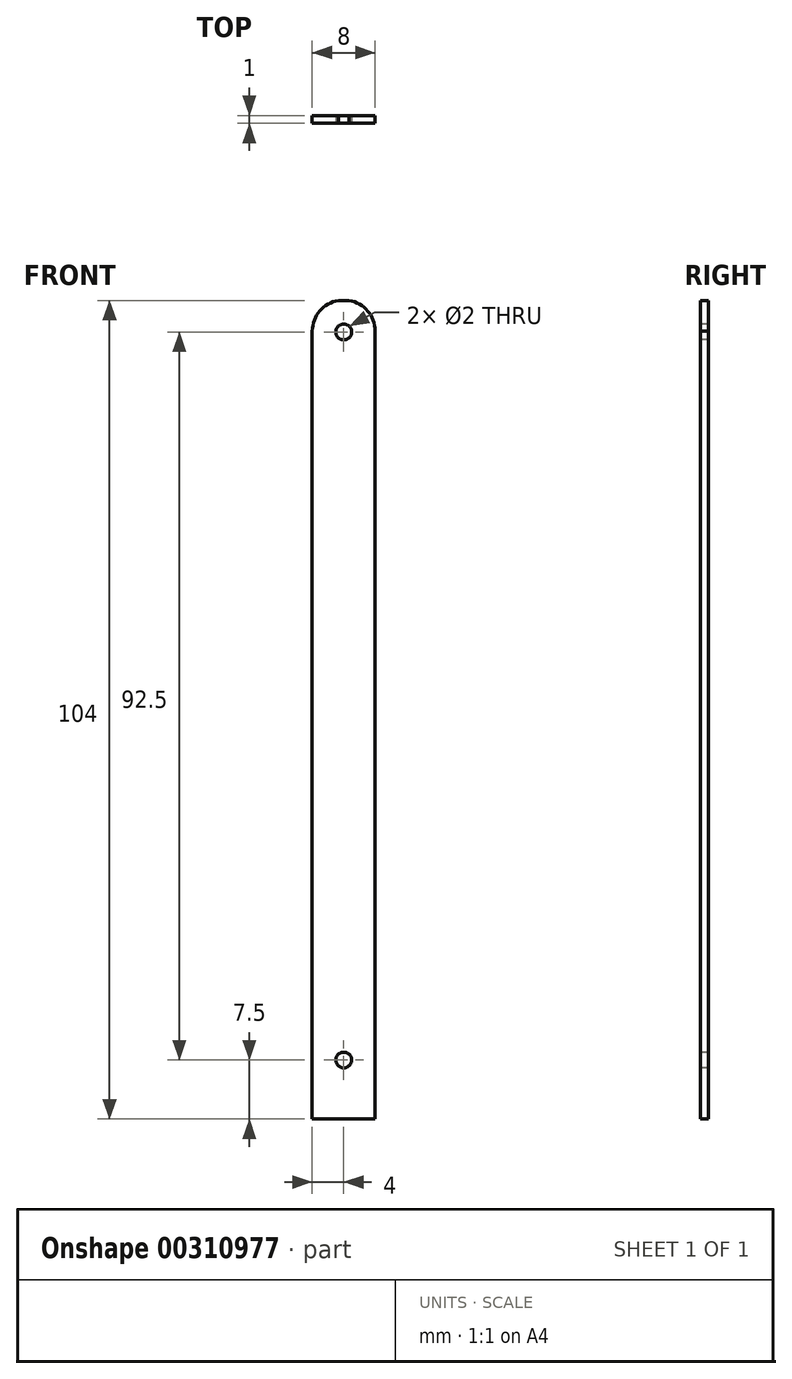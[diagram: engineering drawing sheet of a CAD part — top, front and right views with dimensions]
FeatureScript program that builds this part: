
annotation { "Feature Type Name" : "Feature", "Feature Type Description" : "" }
export const myFeature = defineFeature(function(context is Context, id is Id, definition is map)
    precondition{}
    {
        {
            var Q0;
            Q0=qCreatedBy(makeId("Front.planeOp"),FACE);
            var sketch = newSketch(context, id + "F0", { "sketchPlane" : qUnion([Q0])});
            skLineSegment(sketch, "E0.bottom", {"start": v(4, -52) * mm, "end": v(-4, -52) * mm});
            skLineSegment(sketch, "E0.top", {"start": v(4, 52) * mm, "end": v(-4, 52) * mm});
            skLineSegment(sketch, "E0.left", {"start": v(4, -52) * mm, "end": v(4, 52) * mm});
            skLineSegment(sketch, "E0.right", {"start": v(-4, -52) * mm, "end": v(-4, 52) * mm});
            skPoint(sketch, "E0.middle", {"position": v(0, 0) * mm});
            skLineSegment(sketch, "E1", {"start": v(-4, 48) * mm, "end": v(4, 48) * mm});
            skArc(sketch, "E2", {"start": v(4, 48) * mm, "mid": v(0, 52.06) * mm, "end": v(-4, 48) * mm});
            skSolve(sketch);
        }
        {
            var Q0;
            {var subQ0=sQuery(id+"F0.wireOp",EDGE,"E0.bottom");Q0=makeQuery(id+"F0.imprint","IMPRINT",FACE,{"disambiguationData":[TD([[makeQuery(id+"F0.imprint","IMPRINT",EDGE,{"derivedFrom":subQ0}),-1.0]])]});}
            var Q1;
            {var subQ1=sQuery(id+"F0.wireOp",EDGE,"E1");Q1=makeQuery(id+"F0.imprint","IMPRINT",FACE,{"disambiguationData":[TD([[makeQuery(id+"F0.imprint","IMPRINT",EDGE,{"derivedFrom":subQ1}),1.0]])]});}
            extrude(context, id + "F1", {"entities" : qUnion([Q0, Q1]), "depth" : 1 * mm});
        }
        {
            var Q0;
            Q0=makeQuery(id+"F1.opExtrude","CAP_FACE",FACE,{"disambiguationData":[OSD([sQuery(id+"F0.wireOp",EDGE,"E0.bottom"),sQuery(id+"F0.wireOp",EDGE,"E0.top"),sQuery(id+"F0.wireOp",EDGE,"E0.left"),sQuery(id+"F0.wireOp",EDGE,"E0.right"),sQuery(id+"F0.wireOp",EDGE,"E2")])],"isStart":false});
            var sketch = newSketch(context, id + "F2", { "sketchPlane" : qUnion([Q0])});
            skCircle(sketch, "E3", {"center": v(0, 48) * mm, "radius": 1 * mm});
            skPoint(sketch, "E3.centerSnap0", {"position": v(0, 52) * mm});
            skCircle(sketch, "E4", {"center": v(0, -44.5) * mm, "radius": 1 * mm});
            skSolve(sketch);
        }
        {
            var Q0;
            Q0=makeQuery(id+"F2.imprint","IMPRINT",FACE,{"disambiguationData":[TD([[makeQuery(id+"F2.imprint","IMPRINT",EDGE,{"derivedFrom":sQuery(id+"F2.wireOp",EDGE,"E4")}),1.0]])]});
            var Q1;
            Q1=makeQuery(id+"F2.imprint","IMPRINT",FACE,{"disambiguationData":[TD([[makeQuery(id+"F2.imprint","IMPRINT",EDGE,{"derivedFrom":sQuery(id+"F2.wireOp",EDGE,"E3")}),1.0]])]});
            extrude(context, id + "F3", {"entities" : qUnion([Q0, Q1]), "operationType" : NewBodyOperationType.REMOVE, "endBound" : BoundingType.THROUGH_ALL, "oppositeDirection" : true, "depth" : 25 * mm});
        }
    });
